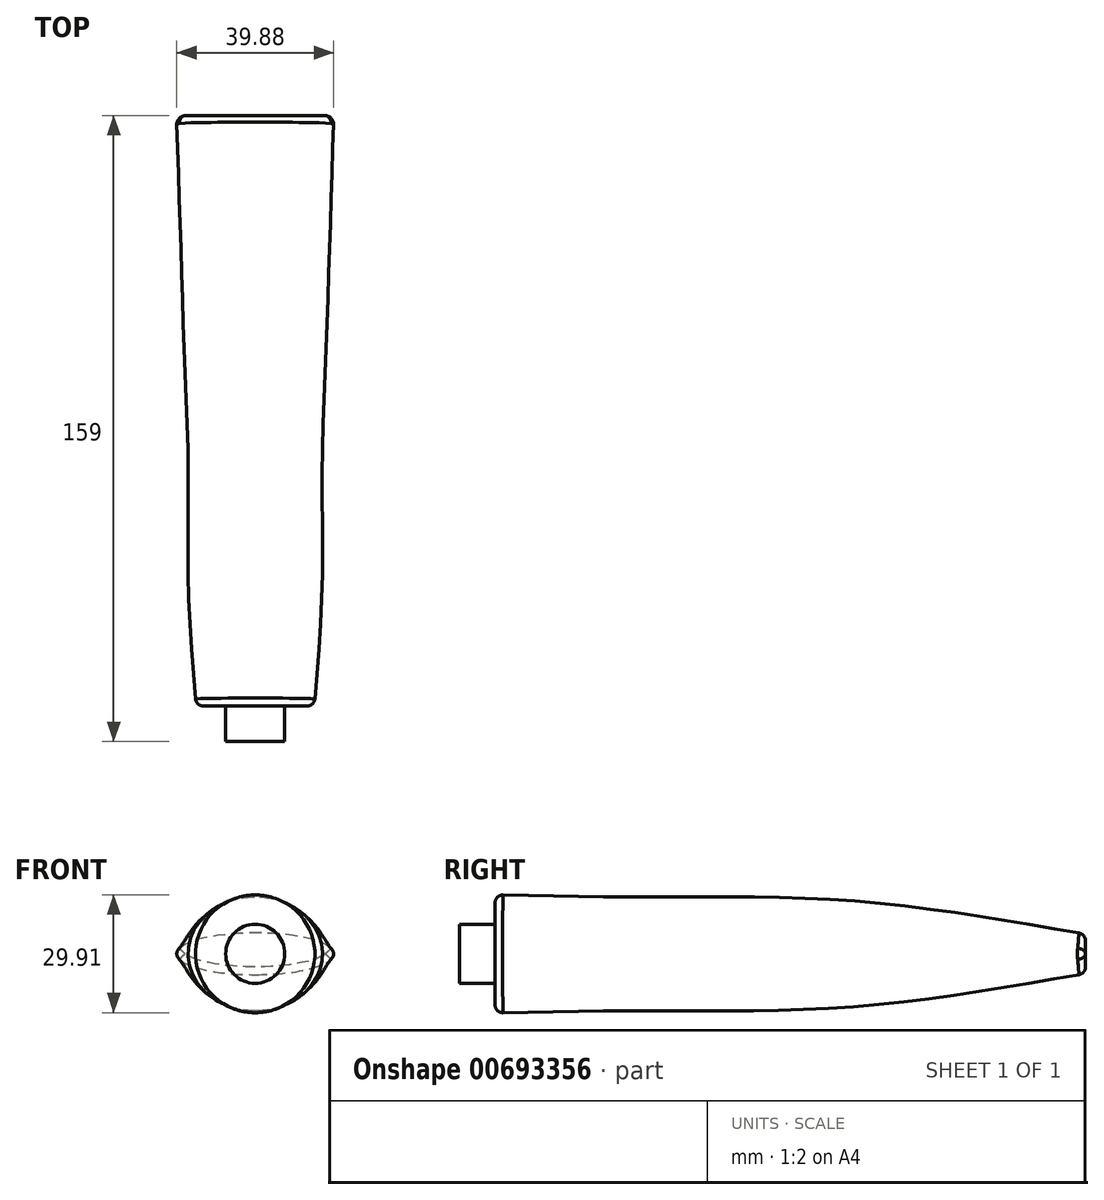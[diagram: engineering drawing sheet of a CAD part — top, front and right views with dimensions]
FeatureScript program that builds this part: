
annotation { "Feature Type Name" : "Feature", "Feature Type Description" : "" }
export const myFeature = defineFeature(function(context is Context, id is Id, definition is map)
    precondition{}
    {
        {
            var Q0;
            Q0=qCreatedBy(makeId("Front.planeOp"),FACE);
            cPlane(context, id + "F0", {"entities" : qUnion([Q0]), "cplaneType" : CPlaneType.OFFSET, "offset" : 30 * mm, "oppositeDirection" : true, "width" : 150 * mm, "height" : 150 * mm});
        }
        {
            var Q0;
            Q0=qCreatedBy(makeId("Front.planeOp"),FACE);
            cPlane(context, id + "F1", {"entities" : qUnion([Q0]), "cplaneType" : CPlaneType.OFFSET, "offset" : 60 * mm, "oppositeDirection" : true, "width" : 150 * mm, "height" : 150 * mm});
        }
        {
            var Q0;
            Q0=qCreatedBy(makeId("Front.planeOp"),FACE);
            cPlane(context, id + "F2", {"entities" : qUnion([Q0]), "cplaneType" : CPlaneType.OFFSET, "offset" : 90 * mm, "oppositeDirection" : true, "width" : 150 * mm, "height" : 150 * mm});
        }
        {
            var Q0;
            Q0=qCreatedBy(makeId("Front.planeOp"),FACE);
            cPlane(context, id + "F3", {"entities" : qUnion([Q0]), "cplaneType" : CPlaneType.OFFSET, "offset" : 120 * mm, "oppositeDirection" : true, "width" : 150 * mm, "height" : 150 * mm});
        }
        {
            var Q0;
            Q0=qCreatedBy(makeId("Front.planeOp"),FACE);
            cPlane(context, id + "F4", {"entities" : qUnion([Q0]), "cplaneType" : CPlaneType.OFFSET, "offset" : 150 * mm, "oppositeDirection" : true, "width" : 150 * mm, "height" : 150 * mm});
        }
        {
            var Q0;
            Q0=qCreatedBy(makeId("Front.planeOp"),FACE);
            var sketch = newSketch(context, id + "F5", { "sketchPlane" : qUnion([Q0])});
            skCircle(sketch, "E0", {"center": v(0, 0) * mm, "radius": 15 * mm});
            skSolve(sketch);
        }
        {
            var Q0;
            Q0=qCreatedBy(id+"F0.planeOp",FACE);
            var sketch = newSketch(context, id + "F6", { "sketchPlane" : qUnion([Q0])});
            skEllipse(sketch, "E1", {"center": v(0, 0) * mm, "majorRadius": 17 * mm, "minorRadius": 14.5 * mm, "majorAxis": v(1, 0)});
            skSolve(sketch);
        }
        {
            var Q0;
            Q0=qCreatedBy(id+"F1.planeOp",FACE);
            var sketch = newSketch(context, id + "F7", { "sketchPlane" : qUnion([Q0])});
            skEllipse(sketch, "E2", {"center": v(0, 0) * mm, "majorRadius": 17 * mm, "minorRadius": 14.5 * mm, "majorAxis": v(1, 0)});
            skSolve(sketch);
        }
        {
            var Q0;
            Q0=qCreatedBy(id+"F2.planeOp",FACE);
            var sketch = newSketch(context, id + "F8", { "sketchPlane" : qUnion([Q0])});
            skEllipse(sketch, "E3", {"center": v(0, 0) * mm, "majorRadius": 18 * mm, "minorRadius": 13.5 * mm, "majorAxis": v(1, 0)});
            skSolve(sketch);
        }
        {
            var Q0;
            Q0=qCreatedBy(id+"F3.planeOp",FACE);
            var sketch = newSketch(context, id + "F9", { "sketchPlane" : qUnion([Q0])});
            skEllipse(sketch, "E4", {"center": v(0, 0) * mm, "majorRadius": 19 * mm, "minorRadius": 10 * mm, "majorAxis": v(1, 0)});
            skSolve(sketch);
        }
        {
            var Q0;
            Q0=qCreatedBy(id+"F4.planeOp",FACE);
            var sketch = newSketch(context, id + "F10", { "sketchPlane" : qUnion([Q0])});
            skEllipse(sketch, "E5", {"center": v(0, 0) * mm, "majorRadius": 20 * mm, "minorRadius": 5 * mm, "majorAxis": v(1, 0)});
            skSolve(sketch);
        }
        {
            var Q0;
            Q0=makeQuery(id+"F5.imprint","IMPRINT",FACE,{"disambiguationData":[TD([[makeQuery(id+"F5.imprint","IMPRINT",EDGE,{"derivedFrom":sQuery(id+"F5.wireOp",EDGE,"E0")}),1.0]])]});
            var Q1;
            Q1=makeQuery(id+"F6.imprint","IMPRINT",FACE,{"disambiguationData":[TD([[makeQuery(id+"F6.imprint","IMPRINT",EDGE,{"derivedFrom":sQuery(id+"F6.wireOp",EDGE,"E1")}),1.0]])]});
            var Q2;
            Q2=makeQuery(id+"F7.imprint","IMPRINT",FACE,{"disambiguationData":[TD([[makeQuery(id+"F7.imprint","IMPRINT",EDGE,{"derivedFrom":sQuery(id+"F7.wireOp",EDGE,"E2")}),1.0]])]});
            var Q3;
            Q3=makeQuery(id+"F8.imprint","IMPRINT",FACE,{"disambiguationData":[TD([[makeQuery(id+"F8.imprint","IMPRINT",EDGE,{"derivedFrom":sQuery(id+"F8.wireOp",EDGE,"E3")}),1.0]])]});
            var Q4;
            Q4=makeQuery(id+"F9.imprint","IMPRINT",FACE,{"disambiguationData":[TD([[makeQuery(id+"F9.imprint","IMPRINT",EDGE,{"derivedFrom":sQuery(id+"F9.wireOp",EDGE,"E4")}),1.0]])]});
            var Q5;
            Q5=makeQuery(id+"F10.imprint","IMPRINT",FACE,{"disambiguationData":[TD([[makeQuery(id+"F10.imprint","IMPRINT",EDGE,{"derivedFrom":sQuery(id+"F10.wireOp",EDGE,"E5")}),1.0]])]});
            loft(context, id + "F11", {"sheetProfilesArray" : [{ "sheetProfileEntities" : qUnion([Q0]) }, { "sheetProfileEntities" : qUnion([Q1]) }, { "sheetProfileEntities" : qUnion([Q2]) }, { "sheetProfileEntities" : qUnion([Q3]) }, { "sheetProfileEntities" : qUnion([Q4]) }, { "sheetProfileEntities" : qUnion([Q5]) }]});
        }
        {
            var Q0;
            Q0=makeQuery(id+"F5.imprint","IMPRINT",FACE,{"disambiguationData":[TD([[makeQuery(id+"F5.imprint","IMPRINT",EDGE,{"derivedFrom":sQuery(id+"F5.wireOp",EDGE,"E0")}),1.0]])]});
            var sketch = newSketch(context, id + "F12", { "sketchPlane" : qUnion([Q0])});
            skCircle(sketch, "E6", {"center": v(0, 0) * mm, "radius": 7.5 * mm});
            skSolve(sketch);
        }
        {
            var Q0;
            Q0 = qSketchRegion(id + "F12", true);
            extrude(context, id + "F13", {"entities" : qUnion([Q0]), "operationType" : NewBodyOperationType.ADD, "depth" : 9 * mm, "offsetDistance" : 25 * mm});
        }
        {
            var Q0;
            Q0=makeQuery(id+"F11.opLoft","MID_CAP_EDGE",EDGE,{"disambiguationData":[OSD([sQuery(id+"F5.wireOp",EDGE,"E0")])],"capPos":0.0});
            fillet(context, id + "F14", {"entities" : qUnion([Q0]), "tangentPropagation" : true, "radius" : 2 * mm, "defaultsChanged" : false, "vertexSettings" : [], "allowEdgeOverflow" : false});
        }
        {
            var Q0;
            Q0=makeQuery(id+"F11.opLoft","MID_CAP_EDGE",EDGE,{"disambiguationData":[OSD([sQuery(id+"F10.wireOp",EDGE,"E5")])],"capPos":5.0});
            fillet(context, id + "F15", {"entities" : qUnion([Q0]), "tangentPropagation" : true, "radius" : 2 * mm, "defaultsChanged" : true, "vertexSettings" : [], "allowEdgeOverflow" : false});
        }
    });
